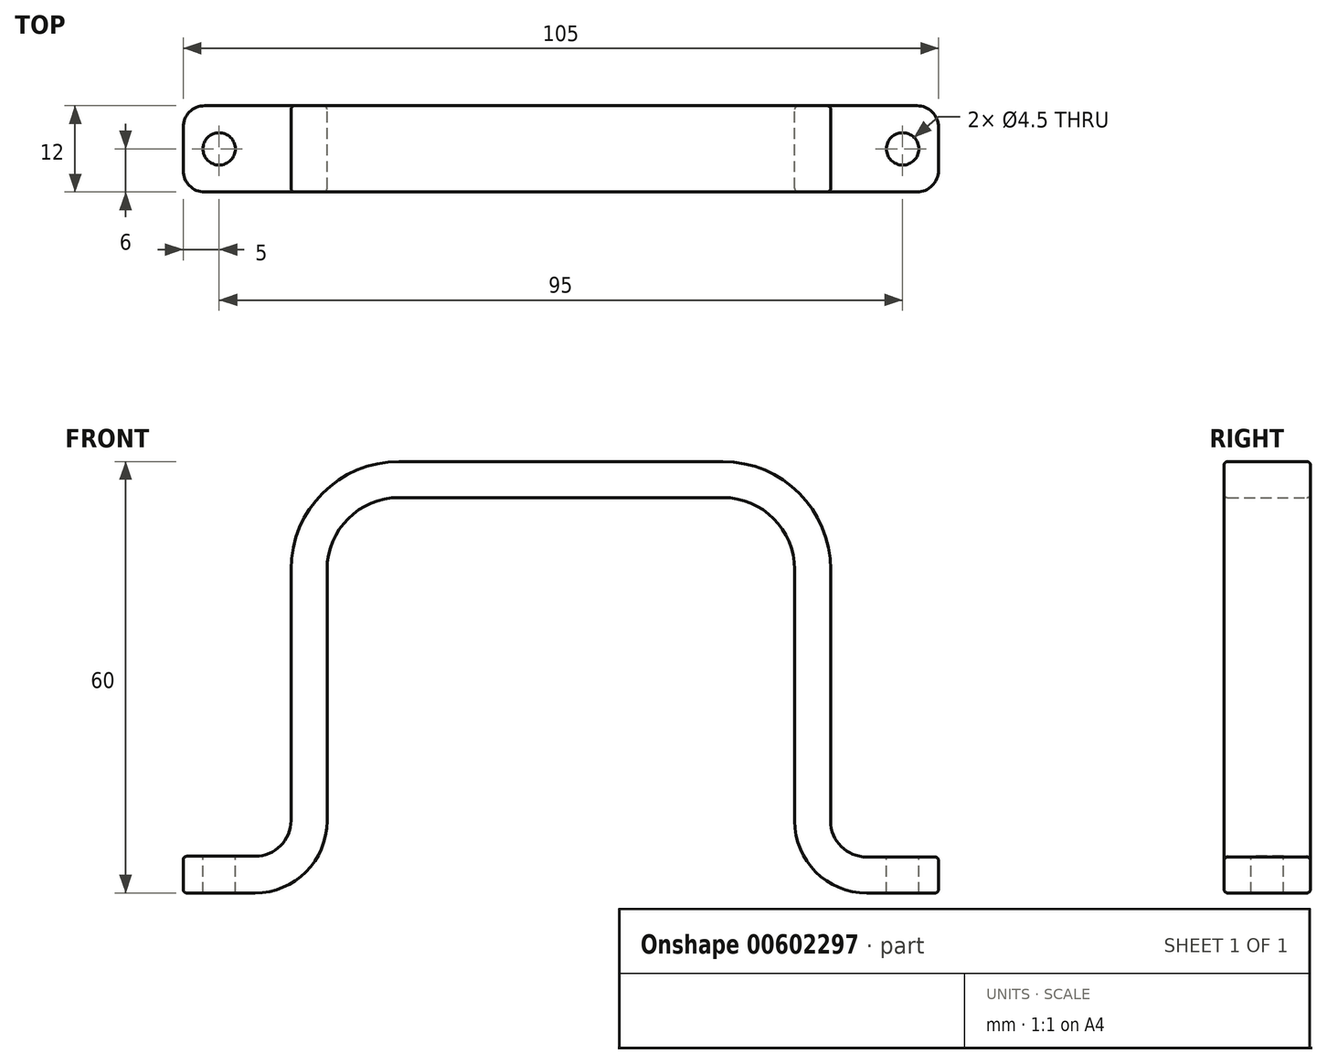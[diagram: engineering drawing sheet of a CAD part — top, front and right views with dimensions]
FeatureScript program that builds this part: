
annotation { "Feature Type Name" : "Feature", "Feature Type Description" : "" }
export const myFeature = defineFeature(function(context is Context, id is Id, definition is map)
    precondition{}
    {
        {
            var Q0;
            Q0=qCreatedBy(makeId("Front.planeOp"),FACE);
            var sketch = newSketch(context, id + "F0", { "sketchPlane" : qUnion([Q0])});
            skLineSegment(sketch, "E0", {"start": v(-52.5, 0) * mm, "end": v(-32.5, 0) * mm});
            skLineSegment(sketch, "E1", {"start": v(-32.5, 0) * mm, "end": v(-32.5, 55) * mm});
            skLineSegment(sketch, "E2", {"start": v(-32.5, 55) * mm, "end": v(32.5, 55) * mm});
            skLineSegment(sketch, "E3", {"start": v(32.5, 55) * mm, "end": v(32.5, 0) * mm});
            skLineSegment(sketch, "E4", {"start": v(32.5, 0) * mm, "end": v(52.5, 0) * mm});
            skLineSegment(sketch, "E5", {"start": v(52.5, 0) * mm, "end": v(52.5, 5) * mm});
            skLineSegment(sketch, "E6", {"start": v(52.5, 5) * mm, "end": v(37.5, 5) * mm});
            skLineSegment(sketch, "E7", {"start": v(37.5, 5) * mm, "end": v(37.5, 60) * mm});
            skLineSegment(sketch, "E8", {"start": v(37.5, 60) * mm, "end": v(-37.5, 60) * mm});
            skLineSegment(sketch, "E9", {"start": v(-37.5, 60) * mm, "end": v(-37.5, 5.1) * mm});
            skLineSegment(sketch, "E10", {"start": v(-37.5, 5.1) * mm, "end": v(-52.5, 5.1) * mm});
            skLineSegment(sketch, "E11", {"start": v(-52.5, 5.1) * mm, "end": v(-52.5, 0) * mm});
            skSolve(sketch);
        }
        {
            var Q0;
            Q0=makeQuery(id+"F0.imprint","IMPRINT",FACE,{"disambiguationData":[TD([[makeQuery(id+"F0.imprint","IMPRINT",EDGE,{"derivedFrom":sQuery(id+"F0.wireOp",EDGE,"E0")}),1.0]])]});
            extrude(context, id + "F1", {"entities" : qUnion([Q0]), "endBound" : BoundingType.SYMMETRIC, "depth" : 12 * mm, "offsetDistance" : 25 * mm});
        }
        {
            var Q0;
            Q0=makeQuery(id+"F1.opExtrude","SWEPT_EDGE",EDGE,{"disambiguationData":[OSD([sQuery(id+"F0.wireOp",EDGE,"E6"),sQuery(id+"F0.wireOp",EDGE,"E7")])]});
            var Q1;
            Q1=makeQuery(id+"F1.opExtrude","SWEPT_EDGE",EDGE,{"disambiguationData":[OSD([sQuery(id+"F0.wireOp",EDGE,"E9"),sQuery(id+"F0.wireOp",EDGE,"E10")])]});
            fillet(context, id + "F2", {"entities" : qUnion([Q0, Q1]), "radius" : 5 * mm, "tangentPropagation" : true, "allowEdgeOverflow" : false});
        }
        {
            var Q0;
            Q0=makeQuery(id+"F1.opExtrude","SWEPT_EDGE",EDGE,{"disambiguationData":[OSD([sQuery(id+"F0.wireOp",EDGE,"E0"),sQuery(id+"F0.wireOp",EDGE,"E1")])]});
            var Q1;
            Q1=makeQuery(id+"F1.opExtrude","SWEPT_EDGE",EDGE,{"disambiguationData":[OSD([sQuery(id+"F0.wireOp",EDGE,"E3"),sQuery(id+"F0.wireOp",EDGE,"E4")])]});
            fillet(context, id + "F3", {"entities" : qUnion([Q0, Q1]), "radius" : 10 * mm, "tangentPropagation" : true, "allowEdgeOverflow" : false});
        }
        {
            var Q0;
            Q0=makeQuery(id+"F1.opExtrude","SWEPT_EDGE",EDGE,{"disambiguationData":[OSD([sQuery(id+"F0.wireOp",EDGE,"E1"),sQuery(id+"F0.wireOp",EDGE,"E2")])]});
            var Q1;
            Q1=makeQuery(id+"F1.opExtrude","SWEPT_EDGE",EDGE,{"disambiguationData":[OSD([sQuery(id+"F0.wireOp",EDGE,"E2"),sQuery(id+"F0.wireOp",EDGE,"E3")])]});
            fillet(context, id + "F4", {"entities" : qUnion([Q0, Q1]), "radius" : 10 * mm, "tangentPropagation" : true, "allowEdgeOverflow" : false});
        }
        {
            var Q0;
            Q0=makeQuery(id+"F1.opExtrude","SWEPT_EDGE",EDGE,{"disambiguationData":[OSD([sQuery(id+"F0.wireOp",EDGE,"E8"),sQuery(id+"F0.wireOp",EDGE,"E9")])]});
            var Q1;
            Q1=makeQuery(id+"F1.opExtrude","SWEPT_EDGE",EDGE,{"disambiguationData":[OSD([sQuery(id+"F0.wireOp",EDGE,"E7"),sQuery(id+"F0.wireOp",EDGE,"E8")])]});
            fillet(context, id + "F5", {"entities" : qUnion([Q0, Q1]), "radius" : 15 * mm, "tangentPropagation" : true, "allowEdgeOverflow" : false});
        }
        {
            var Q0;
            Q0=makeQuery(id+"F1.opExtrude","SWEPT_FACE",FACE,{"disambiguationData":[OSD([sQuery(id+"F0.wireOp",EDGE,"E10")])]});
            var sketch = newSketch(context, id + "F6", { "sketchPlane" : qUnion([Q0])});
            skCircle(sketch, "E12", {"center": v(-47.5, 0) * mm, "radius": 2.25 * mm});
            skPoint(sketch, "E12.centerSnap0", {"position": v(-47.5, -6) * mm});
            skPoint(sketch, "E12.centerSnap1", {"position": v(-52.5, 0) * mm});
            skCircle(sketch, "E13", {"center": v(47.5, 0) * mm, "radius": 2.25 * mm});
            skSolve(sketch);
        }
        {
            var Q0;
            Q0 = qSketchRegion(id + "F6", true);
            extrude(context, id + "F7", {"entities" : qUnion([Q0]), "operationType" : NewBodyOperationType.REMOVE, "endBound" : BoundingType.THROUGH_ALL, "oppositeDirection" : true, "depth" : 25 * mm, "offsetDistance" : 25 * mm});
        }
        {
            var Q0;
            Q0=makeQuery(id+"F1.opExtrude","CAP_EDGE",EDGE,{"disambiguationData":[OSD([sQuery(id+"F0.wireOp",EDGE,"E11")])],"isStart":false});
            var Q1;
            Q1=makeQuery(id+"F1.opExtrude","CAP_EDGE",EDGE,{"disambiguationData":[OSD([sQuery(id+"F0.wireOp",EDGE,"E11")])],"isStart":true});
            var Q2;
            Q2=makeQuery(id+"F1.opExtrude","CAP_EDGE",EDGE,{"disambiguationData":[OSD([sQuery(id+"F0.wireOp",EDGE,"E5")])],"isStart":true});
            var Q3;
            Q3=makeQuery(id+"F1.opExtrude","CAP_EDGE",EDGE,{"disambiguationData":[OSD([sQuery(id+"F0.wireOp",EDGE,"E5")])],"isStart":false});
            fillet(context, id + "F8", {"entities" : qUnion([Q0, Q1, Q2, Q3]), "radius" : 3 * mm, "tangentPropagation" : true, "allowEdgeOverflow" : false});
        }
        {
            var Q0;
            Q0=makeQuery(id+"F1.opExtrude","CAP_EDGE",EDGE,{"disambiguationData":[OSD([sQuery(id+"F0.wireOp",EDGE,"E8")])],"isStart":false});
            var Q1;
            Q1=makeQuery(id+"F1.opExtrude","CAP_EDGE",EDGE,{"disambiguationData":[OSD([sQuery(id+"F0.wireOp",EDGE,"E2")])],"isStart":false});
            fillet(context, id + "F9", {"entities" : qUnion([Q0, Q1]), "radius" : 0.5 * mm, "tangentPropagation" : true, "allowEdgeOverflow" : false});
        }
    });
